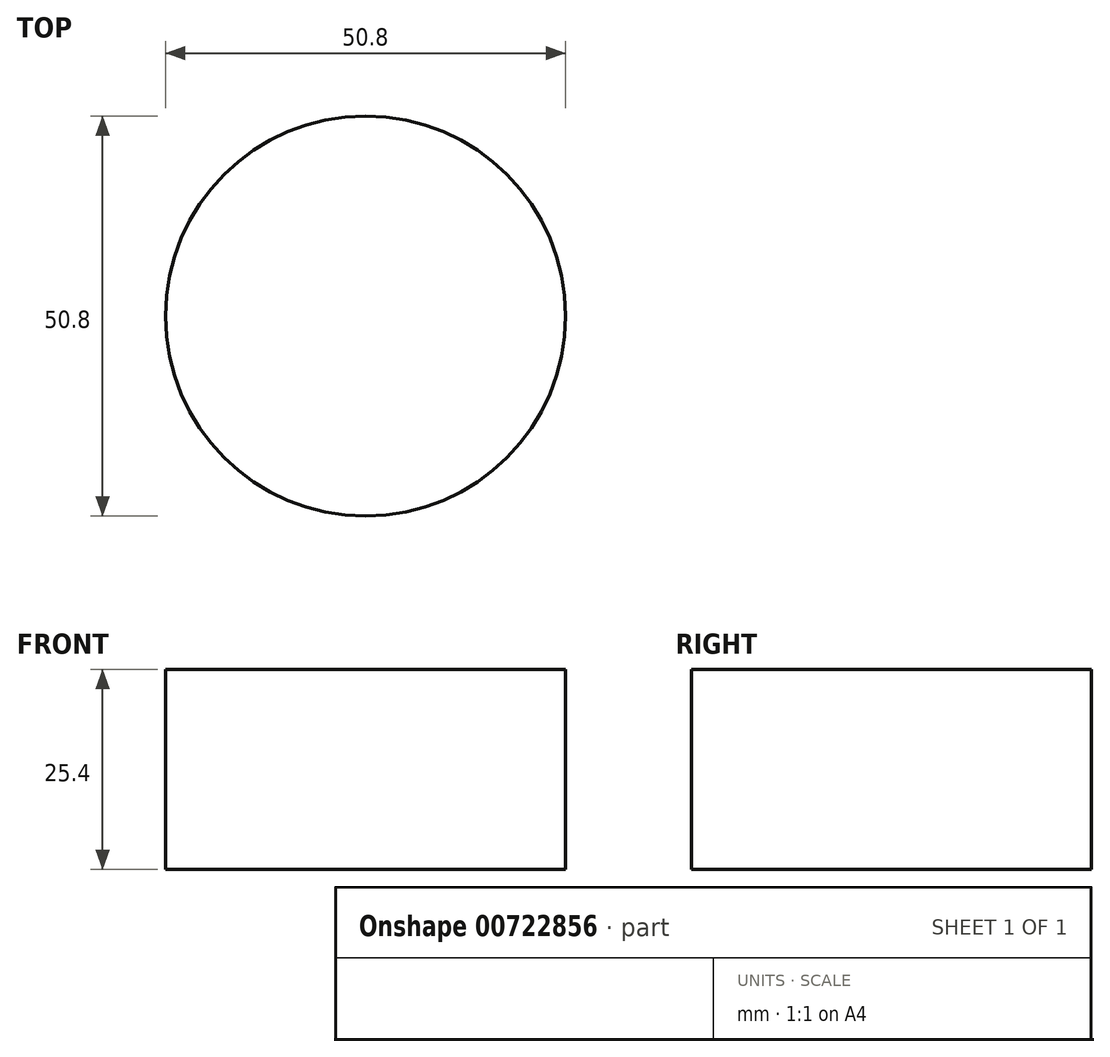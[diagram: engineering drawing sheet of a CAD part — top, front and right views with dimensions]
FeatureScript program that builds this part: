
annotation { "Feature Type Name" : "Feature", "Feature Type Description" : "" }
export const myFeature = defineFeature(function(context is Context, id is Id, definition is map)
    precondition{}
    {
        {
            var Q0;
            Q0=qCreatedBy(makeId("Top.planeOp"),FACE);
            var sketch = newSketch(context, id + "F0", { "sketchPlane" : qUnion([Q0])});
            skCircle(sketch, "E0", {"center": v(0, 0) * mm, "radius": 25.4 * mm});
            skSolve(sketch);
        }
        {
            var Q0;
            Q0=qSketchRegion(id+"F0",true);
            extrude(context, id + "F1", {"entities" : qUnion([Q0]), "depth" : 25.4 * mm, "offsetDistance" : 25.4 * mm});
        }
    });
